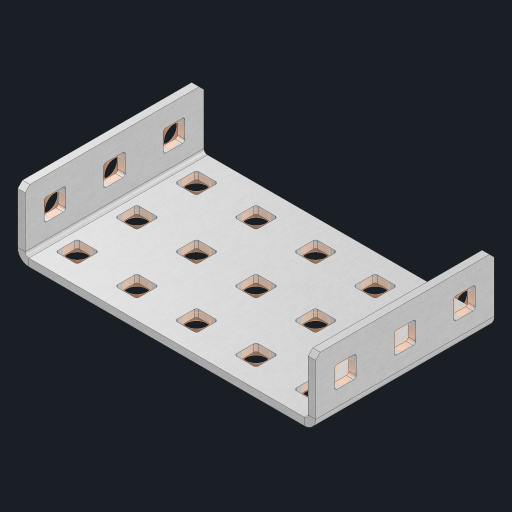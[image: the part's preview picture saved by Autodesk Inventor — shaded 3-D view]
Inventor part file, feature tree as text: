
AUTODESK INVENTOR PART (.ipt)
format: ipt  version: 2023 (Build 270158000, 158)  size: 549,376 bytes
history: native  units: in
note: dims shown in document units (in); Inventor stores cm internally (conversion verified against a paired STEP export)
features: other x26, extrude x20, sheet_metal_op x10, sketch x8, mirror x1, pattern_linear x1, chamfer x1
ambient origin geometry x8: Origin, YZ Plane, XZ Plane, XY Plane, X Axis, Y Axis, Z Axis, Center Point
bodies: Solid1 (feature_tree), Body (feature_tree)
feature tree (67):
  other  "Flange Pattern Plane"
  sheet_metal_op  "Flange Pattern"
  sheet_metal_op  "Body Pattern"
  other  "Arc Length"
  mirror  "Notch Mirror"
  pattern_linear  "Notch Pattern"  Spacing1=0.25in  [1 undecoded]
  chamfer  "End Chamfer"
  extrude  "Half Cut"  Depth=0.0625in
  sketch  "Sketch1"  dims[d0=2.5in]
  other  "Plate1"
  sketch  "Sketch2"  dims[d1=1.5in]
  other  "Plate2"
  sheet_metal_op  "Bend1"
  sheet_metal_op  "Corner1"
  sketch  "Sketch3"  dims[d2=0.0625in]
  other  "Flange Pattern Sketch"
  sketch  "Sketch7"  dims[d3=0.0625in]
  other  "Srf1"
  other  "Srf2"
  sketch  "Sketch8"  dims[d4=0.0312in]
  sketch  "Sketch9"  dims[d5=0.125in]
  other  "Srf91"
  sheet_metal_op  "Body Pattern Sketch"
  other  "Srf92"
  sketch  "Sketch13"  dims[d6=0.0625in]
  sketch  "Sketch14"  dims[d7=0.5in d8=90.0deg d9=0.0312in d10=0.25in d11=0.0625in d12=0.0625in d16=0.182in d17=0.02in d18=0.0625in d19=0.0in d20=0.25in d21=0.25in d46=0.172in d47=1.0in d48=0.0in d49=0.182in d50=0.02in d51=0.25in d52=0.25in d53=0.0625in d54=0.0in d55=0.172in d56=1.0in d57=0.0in d60=1.1811in d62=0.5in d63=1.9685in d65=0.5in d85=0.1473in d86=0.1782in d88=0.04in d89=0.0625in d90=0.0in d91=0.04in d92=0.0491in d95=2.5in d96=0.04in d97=0.25in d98=45.0deg d101=0.0in d102=2.497in d131=2.5in d132=1.1811in d134=0.5in d139=0.5in]
  other  "Srf856"
  other  "Srf1310"
  other  "Srf1311"
  other  "Srf1312"
  other  "Srf1376"
  other  "Srf1377"
  other  "Srf1728"
  other  "Srf1755"
  other  "Srf1942"
  other  "Srf1943"
  other  "Srf1944"
  other  "Srf1945"
  other  "Srf1946"
  other  "Srf1947"
  other  "Srf1948"
  other  "Srf1949"
  other  "Srf1950"
  sheet_metal_op  "Flange Stamp"
  sheet_metal_op  "Flange Circle"
  sheet_metal_op  "Body Stamp"
  sheet_metal_op  "Body Circle"
  sheet_metal_op  "Notch"
  extrude  "ExtrusionSrf2"  Depth=0.0625in
  extrude  "ExtrusionSrf92"  Depth=0.182in
  extrude  "ExtrusionSrf856"  Depth=0.02in
  extrude  "ExtrusionSrf1310"  Depth=0.0625in
  extrude  "ExtrusionSrf1311"  TaperAngle=0.0deg  [1 undecoded]
  extrude  "ExtrusionSrf1312"  Depth=0.25in
  extrude  "ExtrusionSrf1376"  Depth=0.25in
  extrude  "ExtrusionSrf1377"  Depth=0.5in
  extrude  "ExtrusionSrf1728"  Depth=1.0in TaperAngle=0.0deg
  extrude  "ExtrusionSrf1755"  Depth=0.182in
  extrude  "ExtrusionSrf1942"  Depth=0.02in
  extrude  "ExtrusionSrf1943"  Depth=0.25in
  extrude  "ExtrusionSrf1944"  Depth=0.25in
  extrude  "ExtrusionSrf1945"  Depth=0.0625in
  extrude  "ExtrusionSrf1946"  TaperAngle=0.0deg  [1 undecoded]
  extrude  "ExtrusionSrf1947"  Depth=0.5in
  extrude  "ExtrusionSrf1948"  Depth=1.0in TaperAngle=0.0deg
  extrude  "ExtrusionSrf1949"  Depth=1.1811in
  extrude  "ExtrusionSrf1950"  Depth=0.5in
note: 3 required parameter values undecoded (feature->parameter linkage not recoverable at this tier; creation-order binding heuristic only, values carry confidence <= 0.55)
